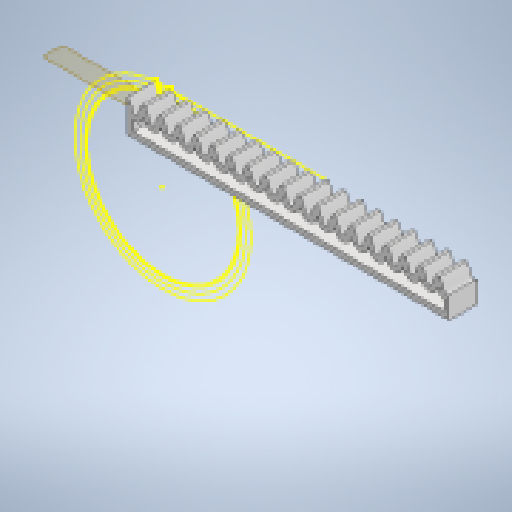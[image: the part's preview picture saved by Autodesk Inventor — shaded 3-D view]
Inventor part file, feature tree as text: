
AUTODESK INVENTOR PART (.ipt)
format: ipt  version: 2023 (Build 270158000, 158)  size: 507,904 bytes
history: native  units: mm
features: other x7, sketch x2, extrude x2, pattern_linear x1, shell x1, reference x1
ambient origin geometry x8: Origin, YZ Plane, XZ Plane, XY Plane, X Axis, Y Axis, Z Axis, Center Point
bodies: Body1 (feature_tree)
feature tree (14):
  other  "rack_V6.ipt"
  other  "Midplane"
  sketch  "Sketch2"  dims[d7=61.768mm d9=2.0mm d10=2.0mm d11=1.0mm d12=5.5mm d13=1.0mm d14=6.5mm d15=0.0mm d16=2.0mm d17=0.0mm d19=0.0mm d20=100.0mm d22=6.283mm d3=20.0mm d4=10.0mm d5=0.0mm d6=10.0mm d8=0.0mm d18=300.0mm d23=6.283mm d24=2.0mm]
  extrude  "Extrusion1"  Depth=20.0mm
  extrude  "Extrusion2"  Depth=10.0mm TaperAngle=0.0deg
  pattern_linear  "Rectangular Pattern1"  Spacing1=10.0mm  [1 undecoded]
  shell  "Shell1"  Thickness=300.0mm
  other  "Solid3::rack_V6.ipt"
  other  "TaggingFeature1"
  sketch  "Sketch1"  dims[d0=10.0mm]
  reference  "Reference1"
  parser-record x1  (decoder bookkeeping rows leaked as tree rows — omitted from the tree; the rows remain in map.json)
  other  "Assembly_V7.iam"
  other  "moulding:1"
note: 1 required parameter value undecoded (feature->parameter linkage not recoverable at this tier; creation-order binding heuristic only, values carry confidence <= 0.55)
note: 1 file-system path scrubbed to <path> (originals preserved in map.json)
